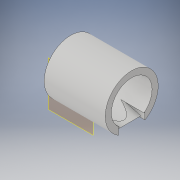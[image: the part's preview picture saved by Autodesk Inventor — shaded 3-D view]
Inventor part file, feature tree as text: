
AUTODESK INVENTOR PART (.ipt)
format: ipt  version: 2019 (Build 230136000, 136)  size: 128,512 bytes
history: native  units: in
note: dims shown in document units (in); Inventor stores cm internally (conversion verified against a paired STEP export)
features: sketch x2, plane x1, revolve x1, extrude x1
ambient origin geometry x8: Origin, YZ Plane, XZ Plane, XY Plane, X Axis, Y Axis, Z Axis, Center Point
bodies: Solid1 (feature_tree)
feature tree (5):
  plane  "Work Plane1"
  revolve  "Revolution1"  [1 undecoded]
  extrude  "Extrusion2"  TaperAngle=90.0deg  [1 undecoded]
  sketch  "Sketch2"  dims[d11=1.1811in d12=0.1181in]
  sketch  "Sketch3"  dims[d13=0.3937in d15=90.0deg d17=0.6693in d19=15.0deg d20=15.0deg d21=0.0984in d23=1.1024in d24=0.1969in d25=0.2091in d26=0.302in d27=0.5118in d28=0.0in]
note: 2 required parameter values undecoded (feature->parameter linkage not recoverable at this tier; creation-order binding heuristic only, values carry confidence <= 0.55)